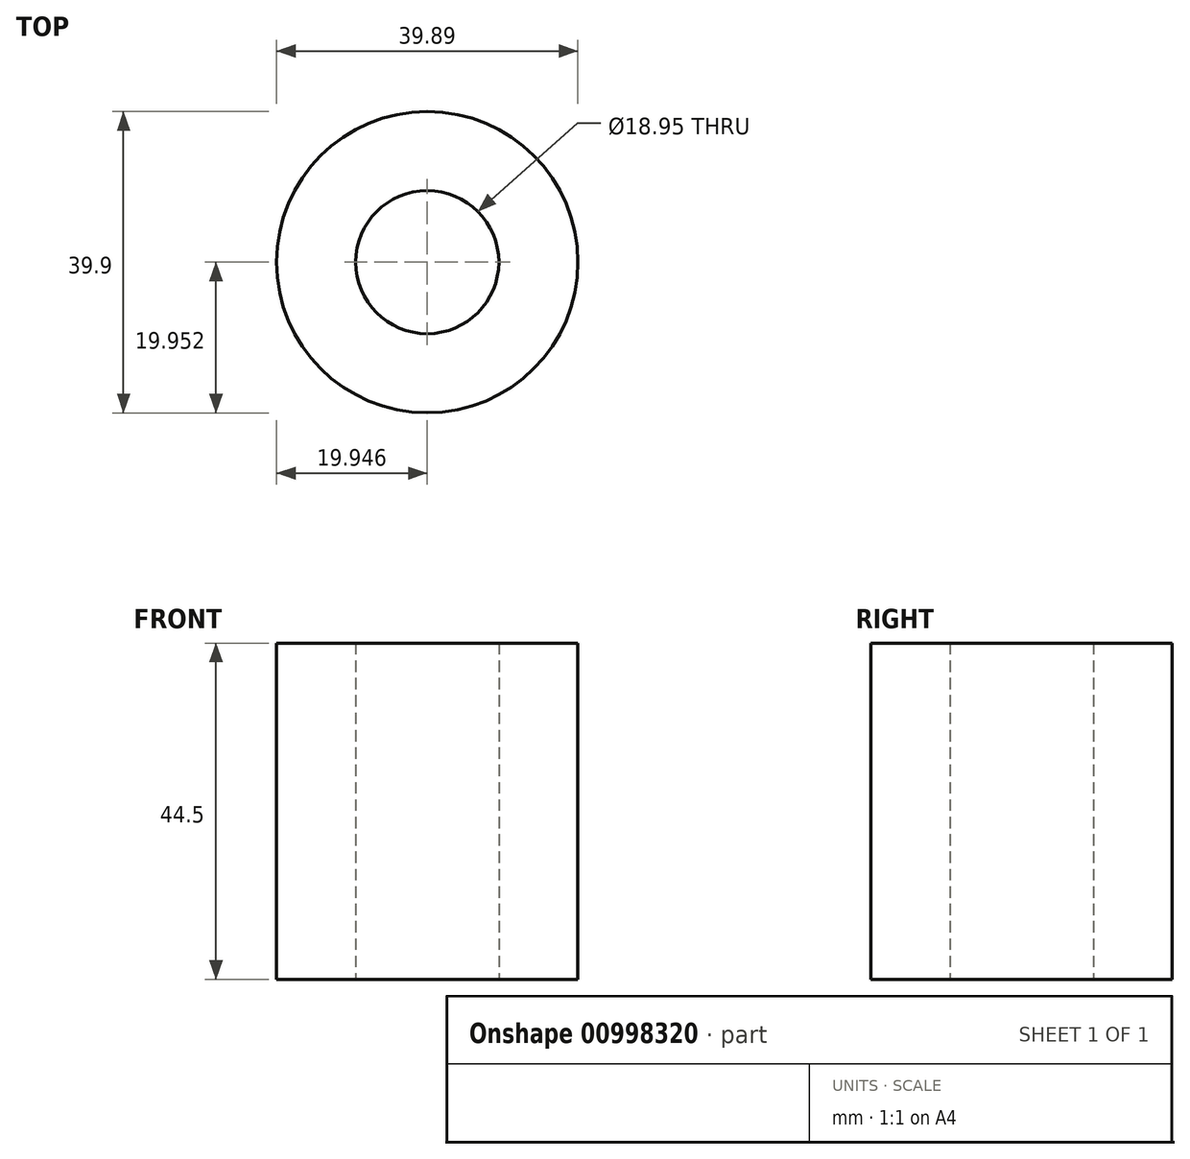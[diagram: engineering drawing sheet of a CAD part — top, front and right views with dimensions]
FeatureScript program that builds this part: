
annotation { "Feature Type Name" : "Feature", "Feature Type Description" : "" }
export const myFeature = defineFeature(function(context is Context, id is Id, definition is map)
    precondition{}
    {
        {
            var Q0;
            Q0=qCreatedBy(makeId("Top.planeOp"),FACE);
            var sketch = newSketch(context, id + "F0", { "sketchPlane" : qUnion([Q0])});
            skCircle(sketch, "E0", {"center": v(-3.35, -28.87) * mm, "radius": 19.95 * mm});
            skCircle(sketch, "E1", {"center": v(-3.35, -28.87) * mm, "radius": 9.47 * mm});
            skSolve(sketch);
        }
        {
            var Q0;
            Q0=makeQuery(id+"F0.imprint","IMPRINT",FACE,{"disambiguationData":[TD([[makeQuery(id+"F0.imprint","IMPRINT",EDGE,{"derivedFrom":sQuery(id+"F0.wireOp",EDGE,"E0")}),1.0]])]});
            extrude(context, id + "F1", {"entities" : qUnion([Q0]), "depth" : 44.5 * mm, "offsetDistance" : 25 * mm});
        }
    });
